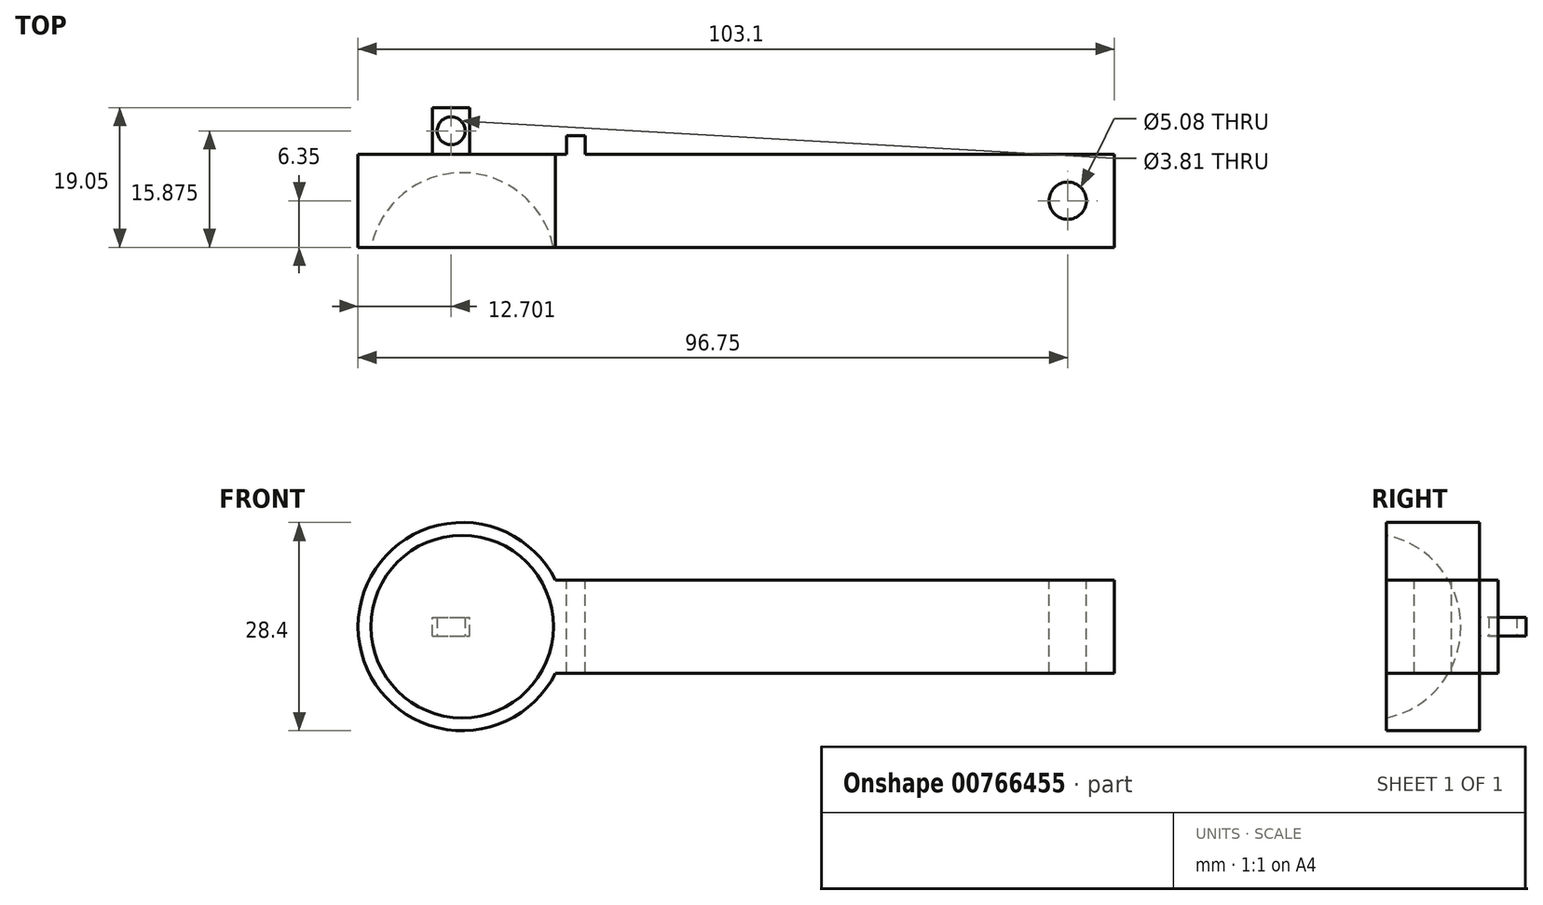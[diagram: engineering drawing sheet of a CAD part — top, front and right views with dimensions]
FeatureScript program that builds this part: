
annotation { "Feature Type Name" : "Feature", "Feature Type Description" : "" }
export const myFeature = defineFeature(function(context is Context, id is Id, definition is map)
    precondition{}
    {
        {
            var Q0;
            Q0=qCreatedBy(makeId("Front.planeOp"),FACE);
            var sketch = newSketch(context, id + "F0", { "sketchPlane" : qUnion([Q0])});
            skLineSegment(sketch, "E0.bottom", {"start": v(38.1, 6.35) * mm, "end": v(-38.1, 6.35) * mm});
            skLineSegment(sketch, "E0.top", {"start": v(38.1, -6.35) * mm, "end": v(-38.1, -6.35) * mm});
            skLineSegment(sketch, "E0.left", {"start": v(38.1, 6.35) * mm, "end": v(38.1, -6.35) * mm});
            skPoint(sketch, "E0.middle", {"position": v(0, 0) * mm});
            skCircle(sketch, "E1", {"center": v(-50.8, 0) * mm, "radius": 14.2 * mm});
            skPoint(sketch, "E1.third.point", {"position": v(-63.5, -6.35) * mm});
            skSolve(sketch);
        }
        {
            var Q0;
            {var subQ0=sQuery(id+"F0.wireOp",EDGE,"E1");var subQ1=makeQuery(id+"F0.imprint","INTERSECT",VERTEX,{"derivedFrom":[sQuery(id+"F0.wireOp",EDGE,"E0.bottom"),subQ0]});Q0=makeQuery(id+"F0.imprint","IMPRINT",FACE,{"disambiguationData":[TD([[makeQuery(id+"F0.imprint","IMPRINT",EDGE,{"disambiguationData":[TD([[subQ1,-1.0]])],"derivedFrom":subQ0}),1.0]])]});}
            extrude(context, id + "F1", {"entities" : qUnion([Q0]), "depth" : 12.7 * mm, "offsetDistance" : 25.4 * mm});
        }
        {
            var Q0;
            Q0=makeQuery(id+"F1.opExtrude","CAP_FACE",FACE,{"disambiguationData":[OSD([sQuery(id+"F0.wireOp",EDGE,"E1")])],"isStart":false});
            cPlane(context, id + "F2", {"entities" : qUnion([Q0]), "cplaneType" : CPlaneType.OFFSET, "offset" : 2.54 * mm, "width" : 152.4 * mm, "height" : 152.4 * mm});
        }
        {
            var Q0;
            Q0=makeQuery(id+"F1.opExtrude","CAP_FACE",FACE,{"disambiguationData":[OSD([sQuery(id+"F0.wireOp",EDGE,"E1")])],"isStart":false});
            var sketch = newSketch(context, id + "F3", { "sketchPlane" : qUnion([Q0])});
            skCircle(sketch, "E2", {"center": v(-50.8, 0) * mm, "radius": 12.7 * mm});
            skSolve(sketch);
        }
        {
            var Q0;
            Q0=qCreatedBy(id+"F2.planeOp",FACE);
            var sketch = newSketch(context, id + "F4", { "sketchPlane" : qUnion([Q0])});
            skCircle(sketch, "E3.0", {"center": v(-50.8, 0) * mm, "radius": 12.7 * mm});
            skLineSegment(sketch, "E4", {"start": v(-69.49, 0) * mm, "end": v(-30.44, 0) * mm});
            skSolve(sketch);
        }
        {
            var Q0;
            {var subQ0=sQuery(id+"F4.wireOp",EDGE,"E4");var subQ1=sQuery(id+"F4.wireOp",EDGE,"E3.0");var subQ2=makeQuery(id+"F4.imprint","INTERSECT",VERTEX,{"disambiguationData":[OD(0.0)],"derivedFrom":[subQ1,subQ0]});Q0=makeQuery(id+"F4.imprint","IMPRINT",FACE,{"disambiguationData":[TD([[makeQuery(id+"F4.imprint","IMPRINT",EDGE,{"disambiguationData":[TD([[subQ2,1.0]])],"derivedFrom":subQ1}),1.0]])]});}
            var Q1;
            Q1=sQuery(id+"F4.wireOp",EDGE,"E4");
            revolve(context, id + "F5", {"operationType" : NewBodyOperationType.REMOVE, "surfaceOperationType" : NewSurfaceOperationType.NEW, "entities" : qUnion([Q0]), "axis" : qUnion([Q1]), "revolveType" : RevolveType.FULL, "oppositeDirection" : true});
        }
        {
            var Q0;
            {var subQ0=sQuery(id+"F0.wireOp",EDGE,"E0.bottom");Q0=makeQuery(id+"F0.imprint","IMPRINT",FACE,{"disambiguationData":[TD([[makeQuery(id+"F0.imprint","IMPRINT",EDGE,{"derivedFrom":subQ0}),1.0]])]});}
            extrude(context, id + "F6", {"entities" : qUnion([Q0]), "operationType" : NewBodyOperationType.ADD, "depth" : 12.7 * mm, "offsetDistance" : 25.4 * mm});
        }
        {
            var Q0;
            Q0=makeQuery(id+"F6.opExtrude","SWEPT_FACE",FACE,{"disambiguationData":[OSD([sQuery(id+"F0.wireOp",EDGE,"E0.bottom")])]});
            var sketch = newSketch(context, id + "F7", { "sketchPlane" : qUnion([Q0])});
            skCircle(sketch, "E5", {"center": v(31.75, -6.35) * mm, "radius": 2.54 * mm});
            skSolve(sketch);
        }
        {
            var Q0;
            Q0=makeQuery(id+"F7.imprint","IMPRINT",FACE,{"disambiguationData":[TD([[makeQuery(id+"F7.imprint","IMPRINT",EDGE,{"derivedFrom":sQuery(id+"F7.wireOp",EDGE,"E5")}),1.0]])]});
            extrude(context, id + "F8", {"entities" : qUnion([Q0]), "operationType" : NewBodyOperationType.REMOVE, "oppositeDirection" : true, "depth" : 12.7 * mm, "offsetDistance" : 25.4 * mm});
        }
        {
            var Q0;
            {var subQ0=sQuery(id+"F0.wireOp",EDGE,"E1");var subQ1=makeQuery(id+"F0.imprint","INTERSECT",VERTEX,{"derivedFrom":[sQuery(id+"F0.wireOp",EDGE,"E0.bottom"),subQ0]});Q0=makeQuery(id+"F0.imprint","IMPRINT",FACE,{"disambiguationData":[TD([[makeQuery(id+"F0.imprint","IMPRINT",EDGE,{"disambiguationData":[TD([[subQ1,-1.0]])],"derivedFrom":subQ0}),1.0]])]});}
            var sketch = newSketch(context, id + "F9", { "sketchPlane" : qUnion([Q0])});
            skLineSegment(sketch, "E6.bottom", {"start": v(-54.84, -1.27) * mm, "end": v(-49.76, -1.27) * mm});
            skLineSegment(sketch, "E6.top", {"start": v(-54.84, 1.27) * mm, "end": v(-49.76, 1.27) * mm});
            skLineSegment(sketch, "E6.left", {"start": v(-54.84, -1.27) * mm, "end": v(-54.84, 1.27) * mm});
            skLineSegment(sketch, "E6.right", {"start": v(-49.76, -1.27) * mm, "end": v(-49.76, 1.27) * mm});
            skPoint(sketch, "E6.middle", {"position": v(-52.3, 0) * mm});
            skSolve(sketch);
        }
        {
            var Q0;
            Q0=makeQuery(id+"F9.imprint","IMPRINT",FACE,{"disambiguationData":[TD([[makeQuery(id+"F9.imprint","IMPRINT",EDGE,{"derivedFrom":sQuery(id+"F9.wireOp",EDGE,"E6.bottom")}),1.0]])]});
            extrude(context, id + "F10", {"entities" : qUnion([Q0]), "operationType" : NewBodyOperationType.ADD, "oppositeDirection" : true, "depth" : 6.35 * mm, "offsetDistance" : 25.4 * mm});
        }
        {
            var Q0;
            Q0=makeQuery(id+"F10.opExtrude","SWEPT_FACE",FACE,{"disambiguationData":[OSD([sQuery(id+"F9.wireOp",EDGE,"E6.bottom")])]});
            var sketch = newSketch(context, id + "F11", { "sketchPlane" : qUnion([Q0])});
            skCircle(sketch, "E7", {"center": v(-52.3, -3.18) * mm, "radius": 1.9 * mm});
            skSolve(sketch);
        }
        {
            var Q0;
            Q0=makeQuery(id+"F11.imprint","IMPRINT",FACE,{"disambiguationData":[TD([[makeQuery(id+"F11.imprint","IMPRINT",EDGE,{"derivedFrom":sQuery(id+"F11.wireOp",EDGE,"E7")}),1.0]])]});
            extrude(context, id + "F12", {"entities" : qUnion([Q0]), "operationType" : NewBodyOperationType.REMOVE, "oppositeDirection" : true, "depth" : 2.54 * mm, "offsetDistance" : 25.4 * mm});
        }
        {
            var Q0;
            {var subQ0=sQuery(id+"F0.wireOp",EDGE,"E0.bottom");Q0=makeQuery(id+"F0.imprint","IMPRINT",FACE,{"disambiguationData":[TD([[makeQuery(id+"F0.imprint","IMPRINT",EDGE,{"derivedFrom":subQ0}),1.0]])]});}
            var sketch = newSketch(context, id + "F13", { "sketchPlane" : qUnion([Q0])});
            skLineSegment(sketch, "E8.bottom", {"start": v(-36.6, -6.35) * mm, "end": v(-34.06, -6.35) * mm});
            skLineSegment(sketch, "E8.top", {"start": v(-36.6, 6.35) * mm, "end": v(-34.06, 6.35) * mm});
            skLineSegment(sketch, "E8.left", {"start": v(-36.6, -6.35) * mm, "end": v(-36.6, 6.35) * mm});
            skLineSegment(sketch, "E8.right", {"start": v(-34.06, -6.35) * mm, "end": v(-34.06, 6.35) * mm});
            skPoint(sketch, "E8.middle", {"position": v(-35.33, 0) * mm});
            skSolve(sketch);
        }
        {
            var Q0;
            Q0=makeQuery(id+"F13.imprint","IMPRINT",FACE,{"disambiguationData":[TD([[makeQuery(id+"F13.imprint","IMPRINT",EDGE,{"derivedFrom":sQuery(id+"F13.wireOp",EDGE,"E8.bottom")}),-1.0]])]});
            extrude(context, id + "F14", {"entities" : qUnion([Q0]), "operationType" : NewBodyOperationType.ADD, "oppositeDirection" : true, "depth" : 2.54 * mm, "offsetDistance" : 25.4 * mm});
        }
    });
